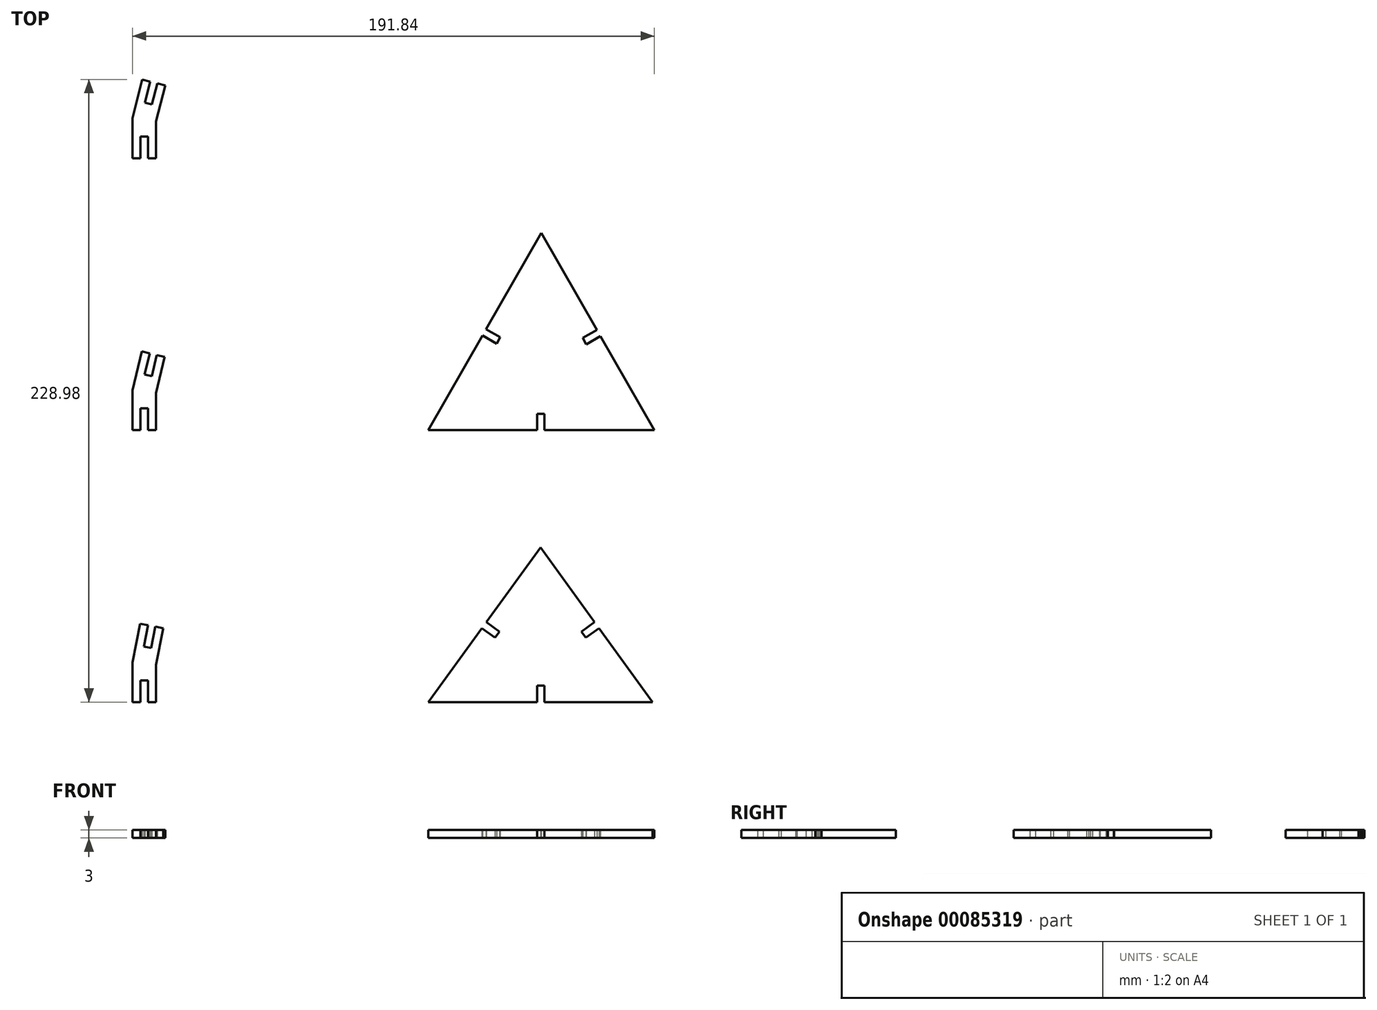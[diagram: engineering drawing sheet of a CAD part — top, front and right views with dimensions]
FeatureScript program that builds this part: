
annotation { "Feature Type Name" : "Feature", "Feature Type Description" : "" }
export const myFeature = defineFeature(function(context is Context, id is Id, definition is map)
    precondition{}
    {
        {
            assignVariable(context, id + "F0", {"name" : "sheet_height", "anyValue" : 3});
        }
        {
            var Q0;
            Q0=qCreatedBy(makeId("Top.planeOp"),FACE);
            var sketch = newSketch(context, id + "F1", { "sketchPlane" : qUnion([Q0])});
            skLineSegment(sketch, "E0", {"start": v(0, 0) * mm, "end": v(83.14, 0) * mm});
            skLineSegment(sketch, "E1", {"start": v(83.14, 0) * mm, "end": v(41.57, 72.5) * mm});
            skLineSegment(sketch, "E2", {"start": v(41.57, 72.5) * mm, "end": v(0, 0) * mm});
            skLineSegment(sketch, "E3", {"start": v(41.57, 72.5) * mm, "end": v(41.57, 0) * mm, "construction": true});
            skLineSegment(sketch, "E4", {"start": v(83.14, 0) * mm, "end": v(20.56, 35.87) * mm, "construction": true});
            skLineSegment(sketch, "E5", {"start": v(0, 0) * mm, "end": v(62.57, 35.87) * mm, "construction": true});
            skLineSegment(sketch, "E6", {"start": v(21.31, 37.17) * mm, "end": v(26.52, 34.19) * mm});
            skLineSegment(sketch, "E7", {"start": v(26.52, 34.19) * mm, "end": v(25.17, 31.85) * mm});
            skLineSegment(sketch, "E8", {"start": v(25.17, 31.85) * mm, "end": v(19.97, 34.83) * mm});
            skLineSegment(sketch, "E9", {"start": v(61.98, 36.91) * mm, "end": v(56.77, 33.93) * mm});
            skLineSegment(sketch, "E10", {"start": v(56.77, 33.93) * mm, "end": v(58.11, 31.59) * mm});
            skLineSegment(sketch, "E11", {"start": v(58.11, 31.59) * mm, "end": v(63.32, 34.57) * mm});
            skLineSegment(sketch, "E12", {"start": v(40.07, 0) * mm, "end": v(40.07, 6) * mm});
            skLineSegment(sketch, "E13", {"start": v(40.07, 6) * mm, "end": v(42.77, 6) * mm});
            skLineSegment(sketch, "E14", {"start": v(42.77, 6) * mm, "end": v(42.77, 0) * mm});
            skSolve(sketch);
        }
        {
            var Q0;
            {var subQ7=sQuery(id+"F1.wireOp",EDGE,"E6");Q0=makeQuery(id+"F1.imprint","IMPRINT",FACE,{"disambiguationData":[TD([[makeQuery(id+"F1.imprint","IMPRINT",EDGE,{"derivedFrom":subQ7}),1.0]])]});}
            extrude(context, id + "F2", {"entities" : qUnion([Q0]), "depth" : (getVariable(context, 'sheet_height')) * mm});
        }
        {
            var Q0;
            Q0=qCreatedBy(makeId("Top.planeOp"),FACE);
            var sketch = newSketch(context, id + "F3", { "sketchPlane" : qUnion([Q0])});
            skLineSegment(sketch, "E15", {"start": v(0, 0) * mm, "end": v(0, -100) * mm, "construction": true});
            skLineSegment(sketch, "E16", {"start": v(0, -100) * mm, "end": v(82.54, -100) * mm});
            skLineSegment(sketch, "E17", {"start": v(82.54, -100) * mm, "end": v(41.27, -43.2) * mm});
            skLineSegment(sketch, "E18", {"start": v(41.27, -43.2) * mm, "end": v(0, -100) * mm});
            skLineSegment(sketch, "E19", {"start": v(41.27, -43.2) * mm, "end": v(41.27, -100) * mm, "construction": true});
            skLineSegment(sketch, "E20", {"start": v(0, -100) * mm, "end": v(54.02, -60.75) * mm, "construction": true});
            skLineSegment(sketch, "E21", {"start": v(82.54, -100) * mm, "end": v(28.52, -60.75) * mm, "construction": true});
            skLineSegment(sketch, "E22", {"start": v(19.75, -72.81) * mm, "end": v(24.6, -76.34) * mm});
            skLineSegment(sketch, "E23", {"start": v(24.6, -76.34) * mm, "end": v(26.2, -74.16) * mm});
            skLineSegment(sketch, "E24", {"start": v(26.2, -74.16) * mm, "end": v(21.34, -70.63) * mm});
            skLineSegment(sketch, "E25", {"start": v(61.2, -70.63) * mm, "end": v(56.34, -74.16) * mm});
            skLineSegment(sketch, "E26", {"start": v(56.34, -74.16) * mm, "end": v(57.93, -76.34) * mm});
            skLineSegment(sketch, "E27", {"start": v(57.93, -76.34) * mm, "end": v(62.78, -72.81) * mm});
            skLineSegment(sketch, "E28", {"start": v(40.07, -100) * mm, "end": v(40.07, -94) * mm});
            skLineSegment(sketch, "E29", {"start": v(40.07, -94) * mm, "end": v(42.77, -94) * mm});
            skLineSegment(sketch, "E30", {"start": v(42.77, -94) * mm, "end": v(42.77, -100) * mm});
            skPoint(sketch, "E31", {"position": v(20.63, -71.6) * mm});
            skPoint(sketch, "E32", {"position": v(61.9, -71.6) * mm});
            skSolve(sketch);
        }
        {
            var Q0;
            {var subQ4=sQuery(id+"F3.wireOp",EDGE,"E22");Q0=makeQuery(id+"F3.imprint","IMPRINT",FACE,{"disambiguationData":[TD([[makeQuery(id+"F3.imprint","IMPRINT",EDGE,{"derivedFrom":subQ4}),-1.0]])]});}
            extrude(context, id + "F4", {"entities" : qUnion([Q0]), "depth" : (getVariable(context, 'sheet_height')) * mm});
        }
        {
            var Q0;
            Q0=qCreatedBy(makeId("Top.planeOp"),FACE);
            var sketch = newSketch(context, id + "F5", { "sketchPlane" : qUnion([Q0])});
            skLineSegment(sketch, "E33", {"start": v(0, 0) * mm, "end": v(-100, 0) * mm, "construction": true});
            skLineSegment(sketch, "E34", {"start": v(-100, 0) * mm, "end": v(-100, 13.64) * mm});
            skLineSegment(sketch, "E35", {"start": v(-103, 0) * mm, "end": v(-100, 0) * mm});
            skLineSegment(sketch, "E36", {"start": v(-103, 0) * mm, "end": v(-103, 8) * mm});
            skLineSegment(sketch, "E37", {"start": v(-103, 8) * mm, "end": v(-105.7, 8) * mm});
            skLineSegment(sketch, "E38", {"start": v(-105.7, 8) * mm, "end": v(-105.7, 0) * mm});
            skLineSegment(sketch, "E39", {"start": v(-105.7, 0) * mm, "end": v(-108.7, 0) * mm});
            skLineSegment(sketch, "E40", {"start": v(-108.7, 0) * mm, "end": v(-108.7, 14.68) * mm});
            skLineSegment(sketch, "E41", {"start": v(-108.7, 14.68) * mm, "end": v(-105.25, 28.95) * mm});
            skLineSegment(sketch, "E42", {"start": v(-105.25, 28.95) * mm, "end": v(-102.33, 28.24) * mm});
            skLineSegment(sketch, "E43", {"start": v(-102.33, 28.24) * mm, "end": v(-104.21, 20.47) * mm});
            skLineSegment(sketch, "E44", {"start": v(-104.21, 20.47) * mm, "end": v(-101.59, 19.83) * mm});
            skLineSegment(sketch, "E45", {"start": v(-101.59, 19.83) * mm, "end": v(-99.7, 27.6) * mm});
            skLineSegment(sketch, "E46", {"start": v(-99.7, 27.6) * mm, "end": v(-96.8, 26.9) * mm});
            skLineSegment(sketch, "E47", {"start": v(-96.8, 26.9) * mm, "end": v(-100, 13.64) * mm});
            skLineSegment(sketch, "E48", {"start": v(-108.7, 14.68) * mm, "end": v(-100, 13.64) * mm, "construction": true});
            skLineSegment(sketch, "E49", {"start": v(-101.59, 19.83) * mm, "end": v(-103, 14) * mm, "construction": true});
            skSolve(sketch);
        }
        {
            var Q0;
            Q0=makeQuery(id+"F5.imprint","IMPRINT",FACE,{"disambiguationData":[TD([[makeQuery(id+"F5.imprint","IMPRINT",EDGE,{"derivedFrom":sQuery(id+"F5.wireOp",EDGE,"E34")}),1.0]])]});
            extrude(context, id + "F6", {"entities" : qUnion([Q0]), "depth" : (getVariable(context, 'sheet_height')) * mm});
        }
        {
            var Q0;
            Q0=qCreatedBy(makeId("Top.planeOp"),FACE);
            var sketch = newSketch(context, id + "F7", { "sketchPlane" : qUnion([Q0])});
            skLineSegment(sketch, "E50", {"start": v(0, -100) * mm, "end": v(-100, -100) * mm, "construction": true});
            skLineSegment(sketch, "E51", {"start": v(-100, -100) * mm, "end": v(-100, -86.3) * mm});
            skLineSegment(sketch, "E52", {"start": v(-103, -100) * mm, "end": v(-100, -100) * mm});
            skLineSegment(sketch, "E53", {"start": v(-103, -100) * mm, "end": v(-103, -92) * mm});
            skLineSegment(sketch, "E54", {"start": v(-103, -92) * mm, "end": v(-105.7, -92) * mm});
            skLineSegment(sketch, "E55", {"start": v(-105.7, -92) * mm, "end": v(-105.7, -100) * mm});
            skLineSegment(sketch, "E56", {"start": v(-105.7, -100) * mm, "end": v(-108.7, -100) * mm});
            skLineSegment(sketch, "E57", {"start": v(-108.7, -100) * mm, "end": v(-108.7, -85.44) * mm});
            skLineSegment(sketch, "E58", {"start": v(-108.7, -85.44) * mm, "end": v(-105.85, -71.15) * mm});
            skLineSegment(sketch, "E59", {"start": v(-105.85, -71.15) * mm, "end": v(-102.9, -71.74) * mm});
            skLineSegment(sketch, "E60", {"start": v(-102.9, -71.74) * mm, "end": v(-104.47, -79.59) * mm});
            skLineSegment(sketch, "E61", {"start": v(-104.47, -79.59) * mm, "end": v(-101.82, -80.12) * mm});
            skLineSegment(sketch, "E62", {"start": v(-101.82, -80.12) * mm, "end": v(-100.26, -72.27) * mm});
            skLineSegment(sketch, "E63", {"start": v(-100.26, -72.27) * mm, "end": v(-97.31, -72.86) * mm});
            skLineSegment(sketch, "E64", {"start": v(-97.31, -72.86) * mm, "end": v(-100, -86.3) * mm});
            skLineSegment(sketch, "E65", {"start": v(-108.7, -85.44) * mm, "end": v(-100, -86.3) * mm, "construction": true});
            skLineSegment(sketch, "E66", {"start": v(-101.82, -80.12) * mm, "end": v(-103, -86) * mm, "construction": true});
            skSolve(sketch);
        }
        {
            var Q0;
            Q0=makeQuery(id+"F7.imprint","IMPRINT",FACE,{"disambiguationData":[TD([[makeQuery(id+"F7.imprint","IMPRINT",EDGE,{"derivedFrom":sQuery(id+"F7.wireOp",EDGE,"E51")}),1.0]])]});
            extrude(context, id + "F8", {"entities" : qUnion([Q0]), "depth" : (getVariable(context, 'sheet_height')) * mm});
        }
        {
            var Q0;
            Q0=qCreatedBy(makeId("Top.planeOp"),FACE);
            var sketch = newSketch(context, id + "F9", { "sketchPlane" : qUnion([Q0])});
            skLineSegment(sketch, "E67", {"start": v(0, 100) * mm, "end": v(-100, 100) * mm, "construction": true});
            skLineSegment(sketch, "E68", {"start": v(-100, 100) * mm, "end": v(-100, 113.62) * mm});
            skLineSegment(sketch, "E69", {"start": v(-103, 100) * mm, "end": v(-100, 100) * mm});
            skLineSegment(sketch, "E70", {"start": v(-103, 100) * mm, "end": v(-103, 108) * mm});
            skLineSegment(sketch, "E71", {"start": v(-103, 108) * mm, "end": v(-105.7, 108) * mm});
            skLineSegment(sketch, "E72", {"start": v(-105.7, 108) * mm, "end": v(-105.7, 100) * mm});
            skLineSegment(sketch, "E73", {"start": v(-105.7, 100) * mm, "end": v(-108.7, 100) * mm});
            skLineSegment(sketch, "E74", {"start": v(-108.7, 100) * mm, "end": v(-108.7, 114.72) * mm});
            skLineSegment(sketch, "E75", {"start": v(-108.7, 114.72) * mm, "end": v(-105.04, 128.98) * mm});
            skLineSegment(sketch, "E76", {"start": v(-105.04, 128.98) * mm, "end": v(-102.13, 128.23) * mm});
            skLineSegment(sketch, "E77", {"start": v(-102.13, 128.23) * mm, "end": v(-104.12, 120.48) * mm});
            skLineSegment(sketch, "E78", {"start": v(-104.12, 120.48) * mm, "end": v(-101.5, 119.81) * mm});
            skLineSegment(sketch, "E79", {"start": v(-101.5, 119.81) * mm, "end": v(-99.52, 127.56) * mm});
            skLineSegment(sketch, "E80", {"start": v(-99.52, 127.56) * mm, "end": v(-96.61, 126.81) * mm});
            skLineSegment(sketch, "E81", {"start": v(-96.61, 126.81) * mm, "end": v(-100, 113.62) * mm});
            skLineSegment(sketch, "E82", {"start": v(-108.7, 114.72) * mm, "end": v(-100, 113.62) * mm, "construction": true});
            skLineSegment(sketch, "E83", {"start": v(-101.5, 119.81) * mm, "end": v(-103, 114) * mm, "construction": true});
            skLineSegment(sketch, "E84", {"start": v(0, 0) * mm, "end": v(0, 100) * mm, "construction": true});
            skSolve(sketch);
        }
        {
            var Q0;
            Q0=makeQuery(id+"F9.imprint","IMPRINT",FACE,{"disambiguationData":[TD([[makeQuery(id+"F9.imprint","IMPRINT",EDGE,{"derivedFrom":sQuery(id+"F9.wireOp",EDGE,"E68")}),1.0]])]});
            extrude(context, id + "F10", {"entities" : qUnion([Q0]), "depth" : (getVariable(context, 'sheet_height')) * mm});
        }
    });
